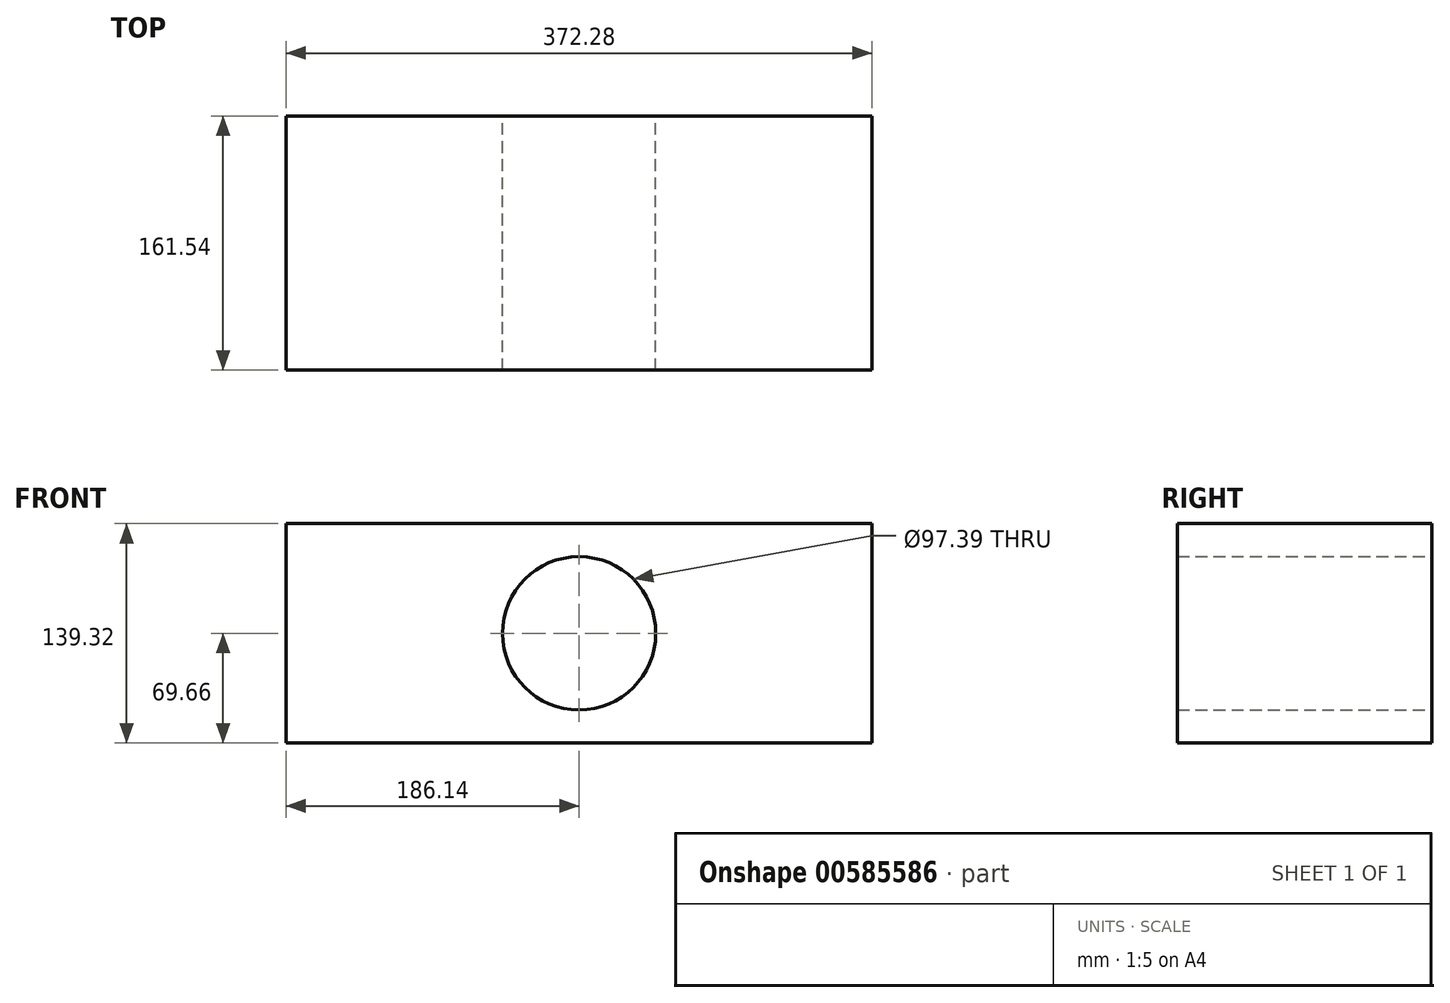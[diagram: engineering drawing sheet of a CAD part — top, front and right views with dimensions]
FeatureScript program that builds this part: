
annotation { "Feature Type Name" : "Feature", "Feature Type Description" : "" }
export const myFeature = defineFeature(function(context is Context, id is Id, definition is map)
    precondition{}
    {
        {
            var Q0;
            Q0=qCreatedBy(makeId("Front.planeOp"),FACE);
            var sketch = newSketch(context, id + "F0", { "sketchPlane" : qUnion([Q0])});
            skLineSegment(sketch, "E0.bottom", {"start": v(-186.14, 69.66) * mm, "end": v(186.14, 69.66) * mm});
            skLineSegment(sketch, "E0.top", {"start": v(-186.14, -69.66) * mm, "end": v(186.14, -69.66) * mm});
            skLineSegment(sketch, "E0.left", {"start": v(-186.14, 69.66) * mm, "end": v(-186.14, -69.66) * mm});
            skLineSegment(sketch, "E0.right", {"start": v(186.14, 69.66) * mm, "end": v(186.14, -69.66) * mm});
            skPoint(sketch, "E0.middle", {"position": v(0, 0) * mm});
            skCircle(sketch, "E1", {"center": v(0, 0) * mm, "radius": 48.7 * mm});
            skSolve(sketch);
        }
        {
            var Q0;
            Q0 = qSketchRegion(id + "F0", true);
            extrude(context, id + "F1", {"entities" : qUnion([Q0]), "endBound" : BoundingType.SYMMETRIC, "depth" : 161.54 * mm, "offsetDistance" : 25.4 * mm});
        }
    });
